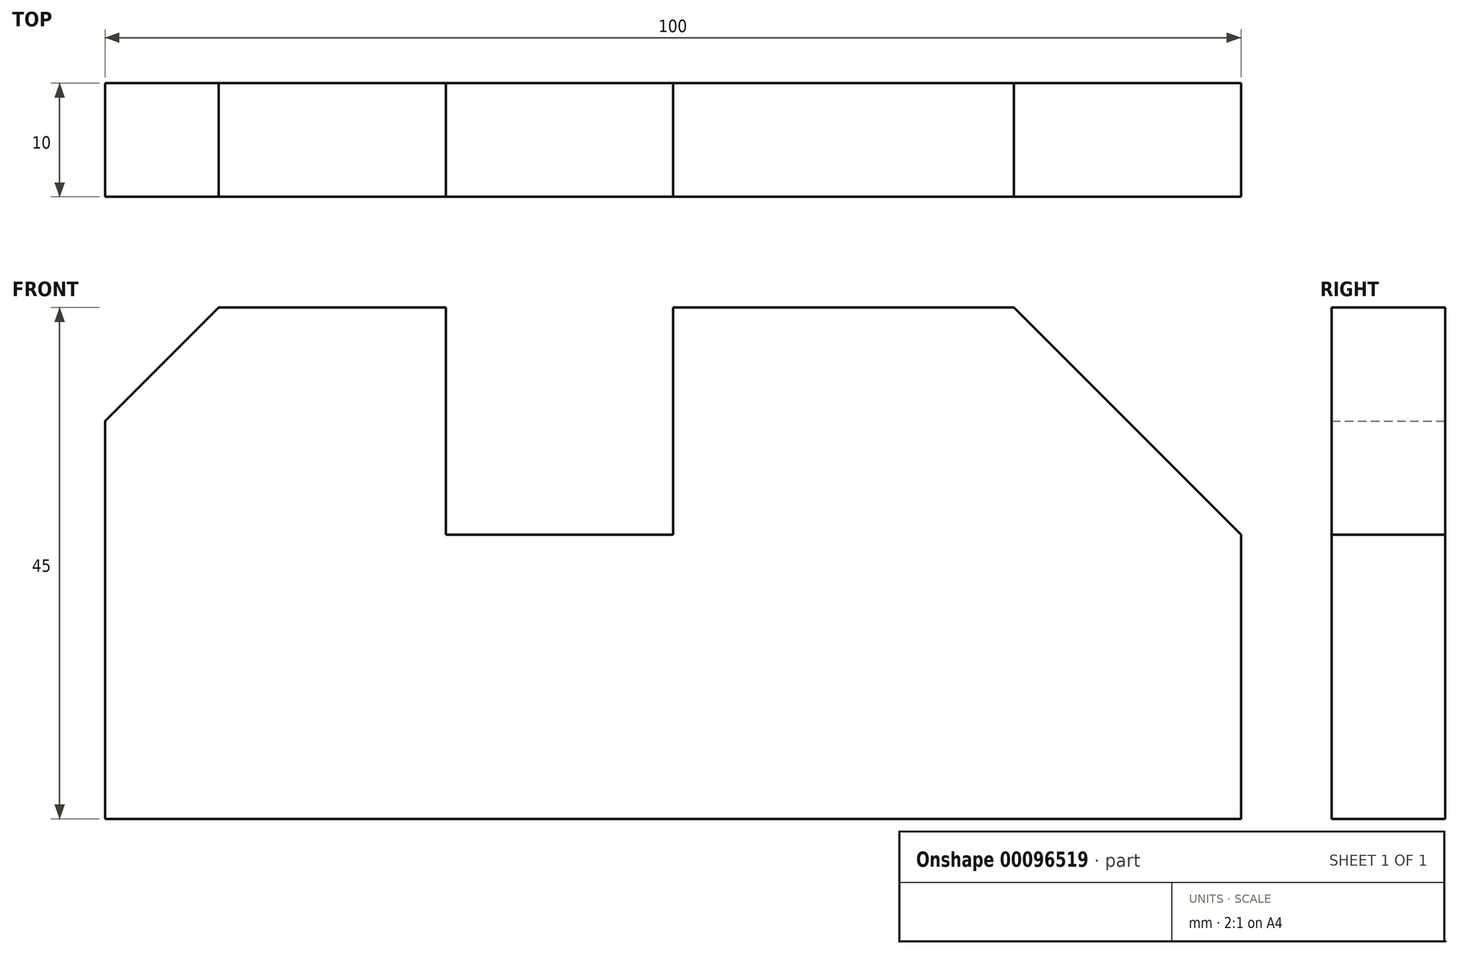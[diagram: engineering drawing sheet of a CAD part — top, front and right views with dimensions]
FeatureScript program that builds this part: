
annotation { "Feature Type Name" : "Feature", "Feature Type Description" : "" }
export const myFeature = defineFeature(function(context is Context, id is Id, definition is map)
    precondition{}
    {
        {
            var Q0;
            Q0=qCreatedBy(makeId("Front.planeOp"),FACE);
            var sketch = newSketch(context, id + "F0", { "sketchPlane" : qUnion([Q0])});
            skLineSegment(sketch, "E0", {"start": v(0, 0) * mm, "end": v(100, 0) * mm});
            skLineSegment(sketch, "E1", {"start": v(0, 0) * mm, "end": v(0, 35) * mm});
            skLineSegment(sketch, "E2", {"start": v(0, 35) * mm, "end": v(10, 45) * mm});
            skLineSegment(sketch, "E3", {"start": v(10, 45) * mm, "end": v(30, 45) * mm});
            skLineSegment(sketch, "E4", {"start": v(30, 45) * mm, "end": v(30, 25) * mm});
            skLineSegment(sketch, "E5", {"start": v(30, 25) * mm, "end": v(50, 25) * mm});
            skLineSegment(sketch, "E6", {"start": v(50, 25) * mm, "end": v(50, 45) * mm});
            skLineSegment(sketch, "E7", {"start": v(100, 0) * mm, "end": v(100, 25) * mm});
            skLineSegment(sketch, "E8", {"start": v(100, 25) * mm, "end": v(80, 45) * mm});
            skLineSegment(sketch, "E9", {"start": v(80, 45) * mm, "end": v(50, 45) * mm});
            skSolve(sketch);
        }
        {
            var Q0;
            Q0 = qSketchRegion(id + "F0", true);
            extrude(context, id + "F1", {"entities" : qUnion([Q0]), "depth" : 10 * mm});
        }
    });
